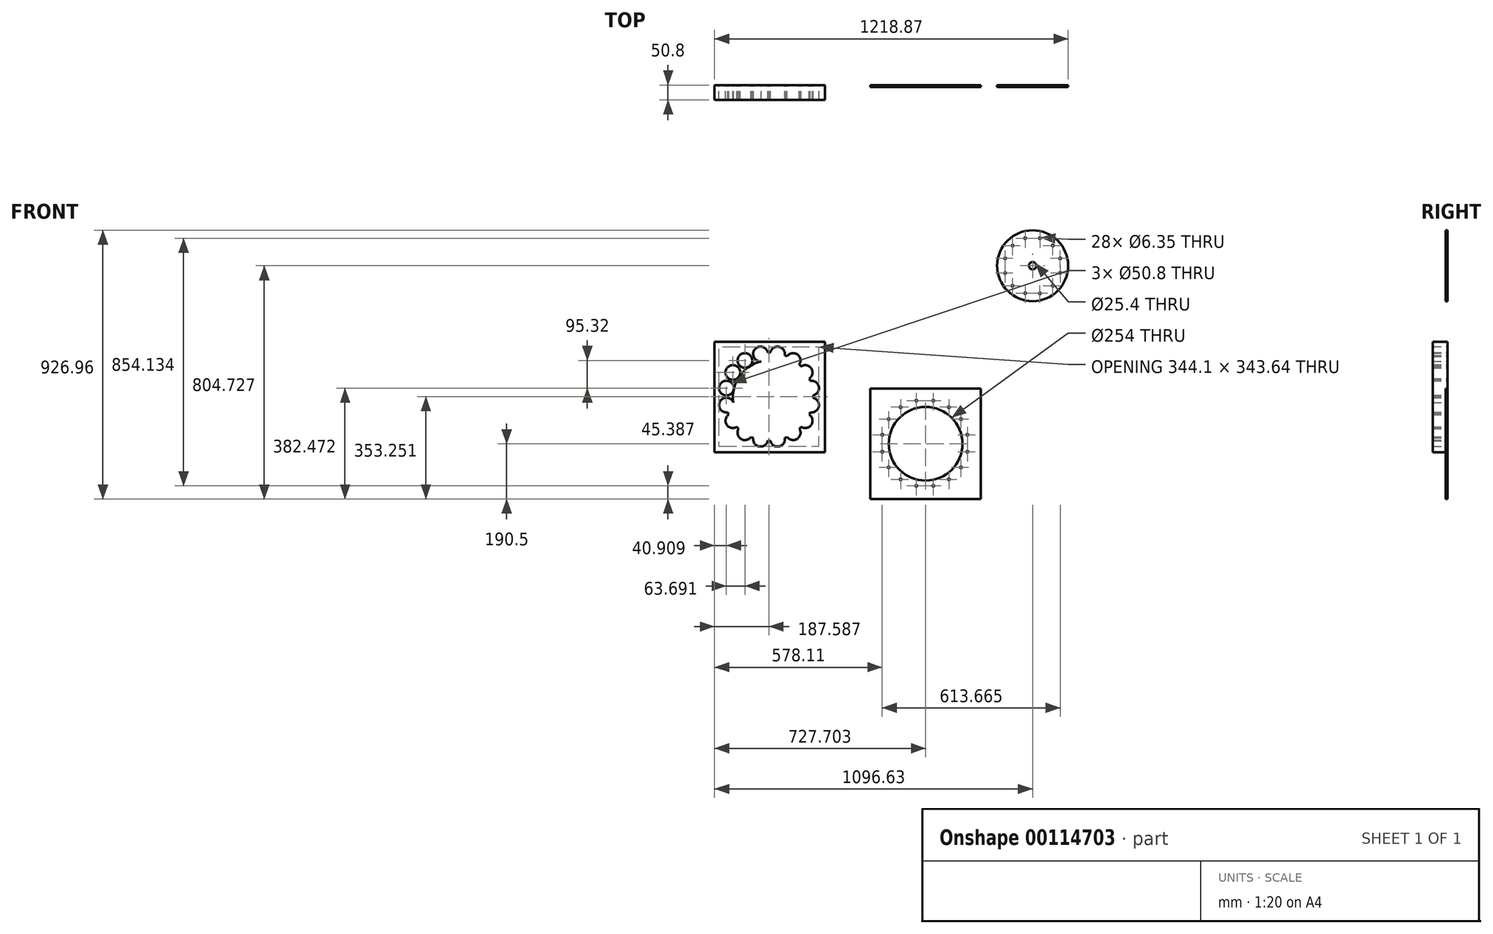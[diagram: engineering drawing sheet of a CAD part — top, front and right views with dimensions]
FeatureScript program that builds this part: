
annotation { "Feature Type Name" : "Feature", "Feature Type Description" : "" }
export const myFeature = defineFeature(function(context is Context, id is Id, definition is map)
    precondition{}
    {
        {
            var Q0;
            Q0=qCreatedBy(makeId("Front.planeOp"),FACE);
            var sketch = newSketch(context, id + "F0", { "sketchPlane" : qUnion([Q0])});
            skCircle(sketch, "E0", {"center": v(0, 0) * mm, "radius": 152.72 * mm});
            skLineSegment(sketch, "E1", {"start": v(0, 152.72) * mm, "end": v(-58.44, 141.1) * mm});
            skLineSegment(sketch, "E2", {"start": v(-58.44, 141.1) * mm, "end": v(-107.99, 107.99) * mm});
            skLineSegment(sketch, "E3", {"start": v(-107.99, 107.99) * mm, "end": v(-141.1, 58.44) * mm});
            skLineSegment(sketch, "E4", {"start": v(-141.1, 58.44) * mm, "end": v(-152.72, 0) * mm});
            skCircle(sketch, "E5", {"center": v(-146.9, 29.22) * mm, "radius": 25.4 * mm});
            skCircle(sketch, "E6", {"center": v(-124.54, 83.22) * mm, "radius": 25.4 * mm});
            skCircle(sketch, "E7", {"center": v(-83.22, 124.54) * mm, "radius": 25.4 * mm});
            skCircle(sketch, "E8", {"center": v(-29.22, 146.9) * mm, "radius": 25.4 * mm});
            skLineSegment(sketch, "E9", {"start": v(-152.72, 0) * mm, "end": v(-141.1, -58.44) * mm});
            skLineSegment(sketch, "E10", {"start": v(-141.1, -58.44) * mm, "end": v(-107.99, -107.99) * mm});
            skLineSegment(sketch, "E11", {"start": v(-107.99, -107.99) * mm, "end": v(-58.44, -141.1) * mm});
            skLineSegment(sketch, "E12", {"start": v(-58.44, -141.1) * mm, "end": v(0, -152.72) * mm});
            skLineSegment(sketch, "E13", {"start": v(0, 152.72) * mm, "end": v(58.44, 141.1) * mm});
            skLineSegment(sketch, "E14", {"start": v(58.44, 141.1) * mm, "end": v(107.99, 107.99) * mm});
            skLineSegment(sketch, "E15", {"start": v(107.99, 107.99) * mm, "end": v(141.1, 58.44) * mm});
            skLineSegment(sketch, "E16", {"start": v(141.1, 58.44) * mm, "end": v(152.72, 0) * mm});
            skLineSegment(sketch, "E17", {"start": v(152.72, 0) * mm, "end": v(141.1, -58.44) * mm});
            skLineSegment(sketch, "E18", {"start": v(141.1, -58.44) * mm, "end": v(107.99, -107.99) * mm});
            skLineSegment(sketch, "E19", {"start": v(107.99, -107.99) * mm, "end": v(58.44, -141.1) * mm});
            skLineSegment(sketch, "E20", {"start": v(58.44, -141.1) * mm, "end": v(0, -152.72) * mm});
            skCircle(sketch, "E21", {"center": v(29.22, 146.9) * mm, "radius": 25.4 * mm});
            skCircle(sketch, "E22", {"center": v(83.22, 124.54) * mm, "radius": 25.4 * mm});
            skCircle(sketch, "E23", {"center": v(124.54, 83.22) * mm, "radius": 25.4 * mm});
            skCircle(sketch, "E24", {"center": v(146.9, 29.22) * mm, "radius": 25.4 * mm});
            skCircle(sketch, "E25", {"center": v(146.9, -29.22) * mm, "radius": 25.4 * mm});
            skCircle(sketch, "E26", {"center": v(124.54, -83.22) * mm, "radius": 25.4 * mm});
            skCircle(sketch, "E27", {"center": v(83.22, -124.54) * mm, "radius": 25.4 * mm});
            skCircle(sketch, "E28", {"center": v(29.22, -146.9) * mm, "radius": 25.4 * mm});
            skCircle(sketch, "E29", {"center": v(-29.22, -146.9) * mm, "radius": 25.4 * mm});
            skCircle(sketch, "E30", {"center": v(-83.22, -124.54) * mm, "radius": 25.4 * mm});
            skCircle(sketch, "E31", {"center": v(-124.54, -83.22) * mm, "radius": 25.4 * mm});
            skCircle(sketch, "E32", {"center": v(-146.9, -29.22) * mm, "radius": 25.4 * mm});
            skCircle(sketch, "E33", {"center": v(0, 0) * mm, "radius": 101.6 * mm});
            skLineSegment(sketch, "E34", {"start": v(0, 101.6) * mm, "end": v(50.8, 87.99) * mm});
            skLineSegment(sketch, "E35", {"start": v(50.8, 87.99) * mm, "end": v(87.99, 50.8) * mm});
            skLineSegment(sketch, "E36", {"start": v(87.99, 50.8) * mm, "end": v(101.6, 0) * mm});
            skLineSegment(sketch, "E37", {"start": v(0, 101.6) * mm, "end": v(-50.8, 87.99) * mm});
            skLineSegment(sketch, "E38", {"start": v(-50.8, 87.99) * mm, "end": v(-87.99, 50.8) * mm});
            skLineSegment(sketch, "E39", {"start": v(-87.99, 50.8) * mm, "end": v(-101.6, 0) * mm});
            skLineSegment(sketch, "E40", {"start": v(-101.6, 0) * mm, "end": v(-87.99, -50.8) * mm});
            skLineSegment(sketch, "E41", {"start": v(-87.99, -50.8) * mm, "end": v(-50.8, -87.99) * mm});
            skLineSegment(sketch, "E42", {"start": v(-50.8, -87.99) * mm, "end": v(0, -101.6) * mm});
            skLineSegment(sketch, "E43", {"start": v(0, -101.6) * mm, "end": v(50.8, -87.99) * mm});
            skLineSegment(sketch, "E44", {"start": v(50.8, -87.99) * mm, "end": v(87.99, -50.8) * mm});
            skLineSegment(sketch, "E45", {"start": v(87.99, -50.8) * mm, "end": v(101.6, 0) * mm});
            skCircle(sketch, "E46", {"center": v(-25.4, -94.8) * mm, "radius": 25.4 * mm});
            skCircle(sketch, "E47", {"center": v(25.4, -94.8) * mm, "radius": 25.4 * mm});
            skCircle(sketch, "E48", {"center": v(69.4, -69.4) * mm, "radius": 25.4 * mm});
            skCircle(sketch, "E49", {"center": v(94.8, -25.4) * mm, "radius": 25.4 * mm});
            skCircle(sketch, "E50", {"center": v(94.8, 25.4) * mm, "radius": 25.4 * mm});
            skCircle(sketch, "E51", {"center": v(69.4, 69.4) * mm, "radius": 25.4 * mm});
            skCircle(sketch, "E52", {"center": v(-69.4, -69.4) * mm, "radius": 25.4 * mm});
            skCircle(sketch, "E53", {"center": v(-94.8, -25.4) * mm, "radius": 25.4 * mm});
            skCircle(sketch, "E54", {"center": v(-94.8, 25.4) * mm, "radius": 25.4 * mm});
            skCircle(sketch, "E55", {"center": v(-69.4, 69.4) * mm, "radius": 25.4 * mm});
            skCircle(sketch, "E56", {"center": v(-25.4, 94.8) * mm, "radius": 25.4 * mm});
            skCircle(sketch, "E57", {"center": v(25.4, 94.8) * mm, "radius": 25.4 * mm});
            skPoint(sketch, "E58", {"position": v(-495.9, 77.2) * mm});
            skLineSegment(sketch, "E59", {"start": v(-495.9, 178.8) * mm, "end": v(-445.1, 165.18) * mm});
            skLineSegment(sketch, "E60", {"start": v(-445.1, 165.18) * mm, "end": v(-407.9, 128) * mm});
            skLineSegment(sketch, "E61", {"start": v(-407.9, 128) * mm, "end": v(-394.3, 77.2) * mm});
            skLineSegment(sketch, "E62", {"start": v(-495.9, 178.8) * mm, "end": v(-546.7, 165.18) * mm});
            skLineSegment(sketch, "E63", {"start": v(-546.7, 165.18) * mm, "end": v(-583.88, 128) * mm});
            skLineSegment(sketch, "E64", {"start": v(-583.88, 128) * mm, "end": v(-597.5, 77.2) * mm});
            skLineSegment(sketch, "E65", {"start": v(-597.5, 77.2) * mm, "end": v(-583.88, 26.4) * mm});
            skLineSegment(sketch, "E66", {"start": v(-583.88, 26.4) * mm, "end": v(-546.7, -10.8) * mm});
            skLineSegment(sketch, "E67", {"start": v(-546.7, -10.8) * mm, "end": v(-495.9, -24.4) * mm});
            skLineSegment(sketch, "E68", {"start": v(-495.9, -24.4) * mm, "end": v(-445.9, -11.25) * mm});
            skLineSegment(sketch, "E69", {"start": v(-445.9, -11.25) * mm, "end": v(-407.2, 27.62) * mm});
            skLineSegment(sketch, "E70", {"start": v(-407.2, 27.62) * mm, "end": v(-394.3, 77.2) * mm});
            skCircle(sketch, "E71", {"center": v(-521.3, -17.6) * mm, "radius": 25.4 * mm});
            skCircle(sketch, "E72", {"center": v(-470.9, -17.83) * mm, "radius": 25.4 * mm});
            skCircle(sketch, "E73", {"center": v(-426.55, 8.19) * mm, "radius": 25.4 * mm});
            skCircle(sketch, "E74", {"center": v(-400.75, 52.4) * mm, "radius": 25.4 * mm});
            skCircle(sketch, "E75", {"center": v(-401.1, 102.6) * mm, "radius": 25.4 * mm});
            skCircle(sketch, "E76", {"center": v(-426.5, 146.59) * mm, "radius": 25.4 * mm});
            skCircle(sketch, "E77", {"center": v(-565.28, 7.8) * mm, "radius": 25.4 * mm});
            skCircle(sketch, "E78", {"center": v(-590.68, 51.8) * mm, "radius": 25.4 * mm});
            skCircle(sketch, "E79", {"center": v(-590.68, 102.6) * mm, "radius": 25.4 * mm});
            skCircle(sketch, "E80", {"center": v(-565.28, 146.59) * mm, "radius": 25.4 * mm});
            skCircle(sketch, "E81", {"center": v(-521.3, 171.99) * mm, "radius": 25.4 * mm});
            skCircle(sketch, "E82", {"center": v(-470.5, 171.99) * mm, "radius": 25.4 * mm});
            skCircle(sketch, "E83", {"center": v(-495.9, 77.2) * mm, "radius": 122.24 * mm});
            skLineSegment(sketch, "E84", {"start": v(-495.9, 77.2) * mm, "end": v(-590.68, 102.6) * mm});
            skLineSegment(sketch, "E85", {"start": v(0, 0) * mm, "end": v(-69.4, 69.4) * mm});
            skCircle(sketch, "E86", {"center": v(0, 0) * mm, "radius": 122.24 * mm});
            skLineSegment(sketch, "E87.bottom", {"start": v(-190.5, -190.5) * mm, "end": v(190.5, -190.5) * mm});
            skLineSegment(sketch, "E87.top", {"start": v(-190.5, 190.5) * mm, "end": v(190.5, 190.5) * mm});
            skLineSegment(sketch, "E87.left", {"start": v(-190.5, -190.5) * mm, "end": v(-190.5, 190.5) * mm});
            skLineSegment(sketch, "E87.right", {"start": v(190.5, -190.5) * mm, "end": v(190.5, 190.5) * mm});
            skCircle(sketch, "E88", {"center": v(0, 0) * mm, "radius": 12.7 * mm});
            skCircle(sketch, "E89", {"center": v(-495.9, 77.2) * mm, "radius": 12.7 * mm});
            skCircle(sketch, "E90", {"center": v(-521.3, 171.99) * mm, "radius": 3.18 * mm});
            skCircle(sketch, "E91", {"center": v(-470.5, 171.99) * mm, "radius": 3.18 * mm});
            skCircle(sketch, "E92", {"center": v(-426.5, 146.59) * mm, "radius": 3.18 * mm});
            skCircle(sketch, "E93", {"center": v(-401.1, 102.6) * mm, "radius": 3.18 * mm});
            skCircle(sketch, "E94", {"center": v(-400.75, 52.4) * mm, "radius": 3.18 * mm});
            skCircle(sketch, "E95", {"center": v(-565.28, 146.59) * mm, "radius": 3.18 * mm});
            skCircle(sketch, "E96", {"center": v(-590.68, 102.6) * mm, "radius": 3.18 * mm});
            skCircle(sketch, "E97", {"center": v(-590.68, 51.8) * mm, "radius": 3.18 * mm});
            skCircle(sketch, "E98", {"center": v(-565.28, 7.8) * mm, "radius": 3.18 * mm});
            skCircle(sketch, "E99", {"center": v(-426.55, 8.19) * mm, "radius": 3.18 * mm});
            skCircle(sketch, "E100", {"center": v(-470.9, -17.83) * mm, "radius": 3.18 * mm});
            skCircle(sketch, "E101", {"center": v(-521.3, -17.6) * mm, "radius": 3.18 * mm});
            skCircle(sketch, "E102", {"center": v(0, 0) * mm, "radius": 127 * mm});
            skLineSegment(sketch, "E103", {"start": v(-539.1, -141.13) * mm, "end": v(-597.55, -152.75) * mm});
            skLineSegment(sketch, "E104", {"start": v(-597.55, -152.75) * mm, "end": v(-647.1, -185.86) * mm});
            skLineSegment(sketch, "E105", {"start": v(-647.1, -185.86) * mm, "end": v(-680.2, -235.4) * mm});
            skLineSegment(sketch, "E106", {"start": v(-680.2, -235.4) * mm, "end": v(-691.82, -293.85) * mm});
            skCircle(sketch, "E107", {"center": v(-686.01, -264.63) * mm, "radius": 25.4 * mm});
            skCircle(sketch, "E108", {"center": v(-663.65, -210.63) * mm, "radius": 25.4 * mm});
            skCircle(sketch, "E109", {"center": v(-622.32, -169.3) * mm, "radius": 25.4 * mm});
            skCircle(sketch, "E110", {"center": v(-568.33, -146.94) * mm, "radius": 25.4 * mm});
            skLineSegment(sketch, "E111", {"start": v(-691.82, -293.85) * mm, "end": v(-680.2, -352.3) * mm});
            skLineSegment(sketch, "E112", {"start": v(-680.2, -352.3) * mm, "end": v(-647.1, -401.84) * mm});
            skLineSegment(sketch, "E113", {"start": v(-647.1, -401.84) * mm, "end": v(-597.55, -434.94) * mm});
            skLineSegment(sketch, "E114", {"start": v(-597.55, -434.94) * mm, "end": v(-539.1, -446.57) * mm});
            skLineSegment(sketch, "E115", {"start": v(-539.1, -141.13) * mm, "end": v(-480.66, -152.75) * mm});
            skLineSegment(sketch, "E116", {"start": v(-480.66, -152.75) * mm, "end": v(-431.11, -185.86) * mm});
            skLineSegment(sketch, "E117", {"start": v(-431.11, -185.86) * mm, "end": v(-398, -235.4) * mm});
            skLineSegment(sketch, "E118", {"start": v(-398, -235.4) * mm, "end": v(-386.38, -293.85) * mm});
            skLineSegment(sketch, "E119", {"start": v(-386.38, -293.85) * mm, "end": v(-398, -352.3) * mm});
            skLineSegment(sketch, "E120", {"start": v(-398, -352.3) * mm, "end": v(-431.11, -401.84) * mm});
            skLineSegment(sketch, "E121", {"start": v(-431.11, -401.84) * mm, "end": v(-480.66, -434.94) * mm});
            skLineSegment(sketch, "E122", {"start": v(-480.66, -434.94) * mm, "end": v(-539.1, -446.57) * mm});
            skCircle(sketch, "E123", {"center": v(-509.88, -146.94) * mm, "radius": 25.4 * mm});
            skCircle(sketch, "E124", {"center": v(-455.89, -169.3) * mm, "radius": 25.4 * mm});
            skCircle(sketch, "E125", {"center": v(-414.56, -210.63) * mm, "radius": 25.4 * mm});
            skCircle(sketch, "E126", {"center": v(-392.2, -264.63) * mm, "radius": 25.4 * mm});
            skCircle(sketch, "E127", {"center": v(-392.2, -323.07) * mm, "radius": 25.4 * mm});
            skCircle(sketch, "E128", {"center": v(-414.56, -377.07) * mm, "radius": 25.4 * mm});
            skCircle(sketch, "E129", {"center": v(-455.89, -418.4) * mm, "radius": 25.4 * mm});
            skCircle(sketch, "E130", {"center": v(-509.88, -440.76) * mm, "radius": 25.4 * mm});
            skCircle(sketch, "E131", {"center": v(-568.33, -440.76) * mm, "radius": 25.4 * mm});
            skCircle(sketch, "E132", {"center": v(-622.32, -418.4) * mm, "radius": 25.4 * mm});
            skCircle(sketch, "E133", {"center": v(-663.65, -377.07) * mm, "radius": 25.4 * mm});
            skCircle(sketch, "E134", {"center": v(-686.01, -323.07) * mm, "radius": 25.4 * mm});
            skPoint(sketch, "E135", {"position": v(-536.42, -295.64) * mm});
            skLineSegment(sketch, "E136.bottom", {"start": v(-726.92, -486.14) * mm, "end": v(-345.92, -486.14) * mm});
            skLineSegment(sketch, "E136.top", {"start": v(-726.92, -105.14) * mm, "end": v(-345.92, -105.14) * mm});
            skLineSegment(sketch, "E136.left", {"start": v(-726.92, -486.14) * mm, "end": v(-726.92, -105.14) * mm});
            skLineSegment(sketch, "E136.right", {"start": v(-345.92, -486.14) * mm, "end": v(-345.92, -105.14) * mm});
            skCircle(sketch, "E137", {"center": v(-536.42, -295.64) * mm, "radius": 127 * mm});
            skCircle(sketch, "E138", {"center": v(-568.33, -146.94) * mm, "radius": 3.18 * mm});
            skCircle(sketch, "E139", {"center": v(-455.89, -169.3) * mm, "radius": 3.18 * mm});
            skCircle(sketch, "E140", {"center": v(-509.88, -146.94) * mm, "radius": 3.18 * mm});
            skCircle(sketch, "E141", {"center": v(-414.56, -210.63) * mm, "radius": 3.17 * mm});
            skCircle(sketch, "E142", {"center": v(-392.2, -264.63) * mm, "radius": 3.18 * mm});
            skCircle(sketch, "E143", {"center": v(-392.2, -323.07) * mm, "radius": 3.18 * mm});
            skCircle(sketch, "E144", {"center": v(-414.56, -377.07) * mm, "radius": 3.18 * mm});
            skCircle(sketch, "E145", {"center": v(-663.65, -210.63) * mm, "radius": 3.18 * mm});
            skCircle(sketch, "E146", {"center": v(-686.01, -264.63) * mm, "radius": 3.18 * mm});
            skCircle(sketch, "E147", {"center": v(-686.01, -323.07) * mm, "radius": 3.18 * mm});
            skCircle(sketch, "E148", {"center": v(-663.65, -377.07) * mm, "radius": 3.18 * mm});
            skCircle(sketch, "E149", {"center": v(-622.32, -418.4) * mm, "radius": 3.18 * mm});
            skCircle(sketch, "E150", {"center": v(-568.33, -440.76) * mm, "radius": 3.18 * mm});
            skCircle(sketch, "E151", {"center": v(-509.88, -440.76) * mm, "radius": 3.18 * mm});
            skCircle(sketch, "E152", {"center": v(-455.89, -418.4) * mm, "radius": 3.18 * mm});
            skCircle(sketch, "E153", {"center": v(-622.32, -169.3) * mm, "radius": 3.18 * mm});
            skLineSegment(sketch, "E154.bottom", {"start": v(-189.72, -647.1) * mm, "end": v(191.28, -647.1) * mm});
            skLineSegment(sketch, "E154.top", {"start": v(-189.72, -266.1) * mm, "end": v(191.28, -266.1) * mm});
            skLineSegment(sketch, "E154.left", {"start": v(-189.72, -647.1) * mm, "end": v(-189.72, -266.1) * mm});
            skLineSegment(sketch, "E154.right", {"start": v(191.28, -647.1) * mm, "end": v(191.28, -266.1) * mm});
            skCircle(sketch, "E155", {"center": v(0.78, -456.6) * mm, "radius": 127 * mm});
            skCircle(sketch, "E156", {"center": v(-31.12, -307.9) * mm, "radius": 3.18 * mm});
            skCircle(sketch, "E157", {"center": v(81.31, -330.26) * mm, "radius": 3.18 * mm});
            skCircle(sketch, "E158", {"center": v(27.32, -307.9) * mm, "radius": 3.18 * mm});
            skCircle(sketch, "E159", {"center": v(122.64, -371.59) * mm, "radius": 3.17 * mm});
            skCircle(sketch, "E160", {"center": v(145, -425.58) * mm, "radius": 3.18 * mm});
            skCircle(sketch, "E161", {"center": v(145, -484.03) * mm, "radius": 3.18 * mm});
            skCircle(sketch, "E162", {"center": v(122.64, -538.02) * mm, "radius": 3.18 * mm});
            skCircle(sketch, "E163", {"center": v(-126.44, -371.59) * mm, "radius": 3.18 * mm});
            skCircle(sketch, "E164", {"center": v(-148.81, -425.58) * mm, "radius": 3.18 * mm});
            skCircle(sketch, "E165", {"center": v(-148.81, -484.03) * mm, "radius": 3.18 * mm});
            skCircle(sketch, "E166", {"center": v(-126.44, -538.02) * mm, "radius": 3.18 * mm});
            skCircle(sketch, "E167", {"center": v(-85.12, -579.35) * mm, "radius": 3.18 * mm});
            skCircle(sketch, "E168", {"center": v(-31.12, -601.71) * mm, "radius": 3.18 * mm});
            skCircle(sketch, "E169", {"center": v(27.32, -601.71) * mm, "radius": 3.18 * mm});
            skCircle(sketch, "E170", {"center": v(81.31, -579.35) * mm, "radius": 3.18 * mm});
            skCircle(sketch, "E171", {"center": v(-85.12, -330.26) * mm, "radius": 3.18 * mm});
            skPoint(sketch, "E172", {"position": v(369.71, 157.63) * mm});
            skCircle(sketch, "E173", {"center": v(369.71, 157.63) * mm, "radius": 122.24 * mm});
            skCircle(sketch, "E174", {"center": v(369.71, 157.63) * mm, "radius": 12.7 * mm});
            skCircle(sketch, "E175", {"center": v(344.31, 252.42) * mm, "radius": 3.18 * mm});
            skCircle(sketch, "E176", {"center": v(395.11, 252.42) * mm, "radius": 3.18 * mm});
            skCircle(sketch, "E177", {"center": v(439.1, 227.02) * mm, "radius": 3.18 * mm});
            skCircle(sketch, "E178", {"center": v(464.5, 183.03) * mm, "radius": 3.18 * mm});
            skCircle(sketch, "E179", {"center": v(464.85, 132.84) * mm, "radius": 3.18 * mm});
            skCircle(sketch, "E180", {"center": v(300.32, 227.02) * mm, "radius": 3.18 * mm});
            skCircle(sketch, "E181", {"center": v(274.92, 183.03) * mm, "radius": 3.18 * mm});
            skCircle(sketch, "E182", {"center": v(274.92, 132.23) * mm, "radius": 3.18 * mm});
            skCircle(sketch, "E183", {"center": v(300.32, 88.23) * mm, "radius": 3.18 * mm});
            skCircle(sketch, "E184", {"center": v(439.05, 88.62) * mm, "radius": 3.18 * mm});
            skCircle(sketch, "E185", {"center": v(394.7, 62.6) * mm, "radius": 3.18 * mm});
            skCircle(sketch, "E186", {"center": v(344.31, 62.83) * mm, "radius": 3.18 * mm});
            skSolve(sketch);
        }
        {
            var Q0;
            Q0=makeQuery(id+"F0.imprint","IMPRINT",FACE,{"disambiguationData":[TD([[makeQuery(id+"F0.imprint","IMPRINT",EDGE,{"derivedFrom":sQuery(id+"F0.wireOp",EDGE,"E154.bottom")}),1.0]])]});
            extrude(context, id + "F1", {"entities" : qUnion([Q0]), "depth" : 6.35 * mm});
        }
        {
            var Q0;
            Q0=makeQuery(id+"F0.imprint","IMPRINT",FACE,{"disambiguationData":[TD([[makeQuery(id+"F0.imprint","IMPRINT",EDGE,{"derivedFrom":sQuery(id+"F0.wireOp",EDGE,"E173")}),1.0]])]});
            extrude(context, id + "F2", {"entities" : qUnion([Q0]), "depth" : 6.35 * mm});
        }
        {
            var Q0;
            {var subQ0=sQuery(id+"F0.wireOp",EDGE,"E110");var subQ1=sQuery(id+"F0.wireOp",EDGE,"E103");var subQ2=makeQuery(id+"F0.imprint","INTERSECT",VERTEX,{"disambiguationData":[OD(0.0)],"derivedFrom":[subQ1,subQ0]});Q0=makeQuery(id+"F0.imprint","IMPRINT",FACE,{"disambiguationData":[TD([[makeQuery(id+"F0.imprint","IMPRINT",EDGE,{"disambiguationData":[TD([[subQ2,-1.0]])],"derivedFrom":subQ1}),-1.0]])]});}
            var Q1;
            {var subQ0=sQuery(id+"F0.wireOp",EDGE,"E110");var subQ1=sQuery(id+"F0.wireOp",EDGE,"E103");var subQ2=makeQuery(id+"F0.imprint","INTERSECT",VERTEX,{"disambiguationData":[OD(0.0)],"derivedFrom":[subQ1,subQ0]});Q1=makeQuery(id+"F0.imprint","IMPRINT",FACE,{"disambiguationData":[TD([[makeQuery(id+"F0.imprint","IMPRINT",EDGE,{"disambiguationData":[TD([[subQ2,-1.0]])],"derivedFrom":subQ1}),1.0]])]});}
            extrude(context, id + "F3", {"entities" : qUnion([Q0, Q1]), "depth" : 50.8 * mm});
        }
    });
